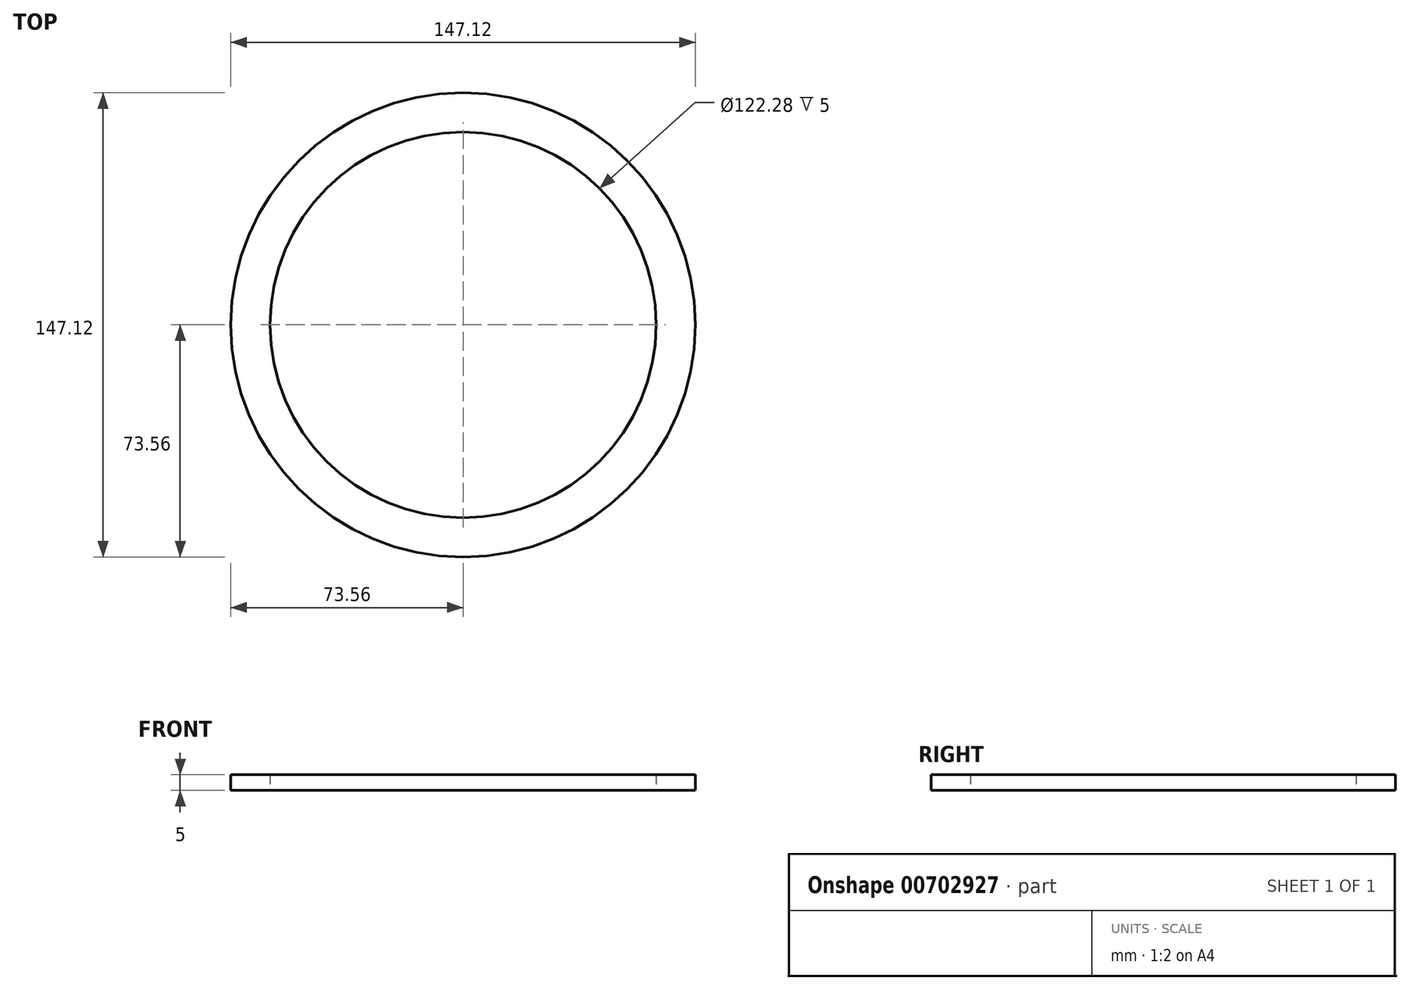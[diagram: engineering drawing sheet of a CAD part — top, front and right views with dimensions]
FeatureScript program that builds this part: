
annotation { "Feature Type Name" : "Feature", "Feature Type Description" : "" }
export const myFeature = defineFeature(function(context is Context, id is Id, definition is map)
    precondition{}
    {
        {
            var Q0;
            Q0=qCreatedBy(makeId("Top.planeOp"),FACE);
            var sketch = newSketch(context, id + "F0", { "sketchPlane" : qUnion([Q0])});
            skCircle(sketch, "E0", {"center": v(0, 0) * mm, "radius": 73.56 * mm});
            skCircle(sketch, "E1", {"center": v(0, 0) * mm, "radius": 61.14 * mm});
            skCircle(sketch, "E2", {"center": v(0, 0) * mm, "radius": 28.12 * mm});
            skCircle(sketch, "E3", {"center": v(0, 0) * mm, "radius": 14.92 * mm});
            skSolve(sketch);
        }
        {
            var Q0;
            Q0=makeQuery(id+"F0.imprint","IMPRINT",FACE,{"disambiguationData":[TD([[makeQuery(id+"F0.imprint","IMPRINT",EDGE,{"derivedFrom":sQuery(id+"F0.wireOp",EDGE,"E0")}),1.0]])]});
            extrude(context, id + "F1", {"entities" : qUnion([Q0]), "depth" : 5 * mm, "offsetDistance" : 25.4 * mm});
        }
    });
